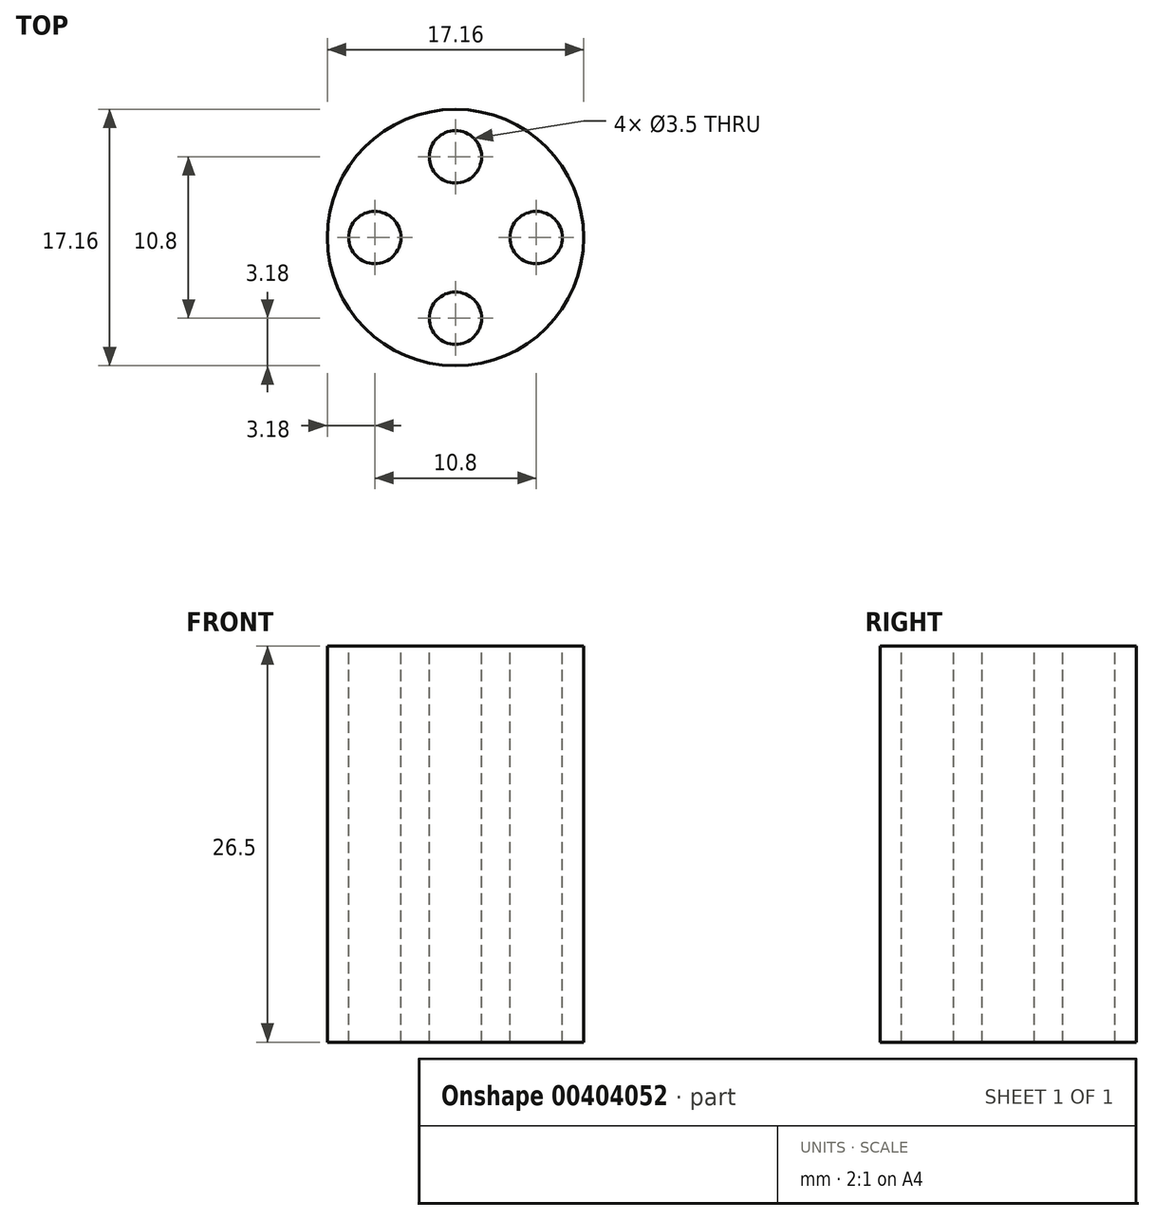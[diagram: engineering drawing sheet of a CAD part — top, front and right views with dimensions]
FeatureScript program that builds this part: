
annotation { "Feature Type Name" : "Feature", "Feature Type Description" : "" }
export const myFeature = defineFeature(function(context is Context, id is Id, definition is map)
    precondition{}
    {
        {
            var Q0;
            Q0=qCreatedBy(makeId("Top.planeOp"),FACE);
            var sketch = newSketch(context, id + "F0", { "sketchPlane" : qUnion([Q0])});
            skCircle(sketch, "E0", {"center": v(0, 0) * mm, "radius": 8.57 * mm});
            skSolve(sketch);
        }
        {
            var Q0;
            Q0 = qSketchRegion(id + "F0", true);
            var Q1;
            Q1=makeQuery(id+"F0.imprint","IMPRINT",FACE,{"disambiguationData":[TD([[makeQuery(id+"F0.imprint","IMPRINT",EDGE,{"derivedFrom":sQuery(id+"F0.wireOp",EDGE,"E0")}),1.0]])]});
            extrude(context, id + "F1", {"entities" : qUnion([Q0, Q1]), "depth" : 26.5 * mm});
        }
        {
            var Q0;
            Q0=makeQuery(id+"F1.opExtrude","CAP_FACE",FACE,{"disambiguationData":[OSD([sQuery(id+"F0.wireOp",EDGE,"E0")])],"isStart":false});
            var sketch = newSketch(context, id + "F2", { "sketchPlane" : qUnion([Q0])});
            skCircle(sketch, "E1", {"center": v(-5.4, 0) * mm, "radius": 0.4 * mm});
            skCircle(sketch, "E2", {"center": v(0, 5.4) * mm, "radius": 0.4 * mm});
            skCircle(sketch, "E3", {"center": v(5.4, 0) * mm, "radius": 0.4 * mm});
            skCircle(sketch, "E4", {"center": v(0, -5.4) * mm, "radius": 0.4 * mm});
            skSolve(sketch);
        }
        {
            var Q0;
            Q0=sQuery(id+"F2.wireOp",VERTEX,"E2.center");
            var Q1;
            Q1=makeQuery(id+"F1.opExtrude","SWEPT_BODY",BODY,{"disambiguationData":[OSD([sQuery(id+"F0.wireOp",EDGE,"E0")])]});
            hole(context, id + "F3", {"style" : HoleStyle.SIMPLE, "endStyle" : HoleEndStyle.THROUGH, "holeDiameter" : 3.5 * mm, "isTappedThrough" : true, "tappedDepth" : 12.7 * mm, "tapClearance" : 3, "locations" : qUnion([Q0]), "scope" : qUnion([Q1])});
        }
        {
            var Q0;
            Q0=sQuery(id+"F2.wireOp",VERTEX,"E3.center");
            var Q1;
            Q1=makeQuery(id+"F1.opExtrude","SWEPT_BODY",BODY,{"disambiguationData":[OSD([sQuery(id+"F0.wireOp",EDGE,"E0")])]});
            hole(context, id + "F4", {"style" : HoleStyle.SIMPLE, "endStyle" : HoleEndStyle.THROUGH, "holeDiameter" : 3.5 * mm, "isTappedThrough" : true, "tappedDepth" : 12.7 * mm, "tapClearance" : 3, "locations" : qUnion([Q0]), "scope" : qUnion([Q1])});
        }
        {
            var Q0;
            Q0=sQuery(id+"F2.wireOp",VERTEX,"E1.center");
            var Q1;
            Q1=sQuery(id+"F2.wireOp",VERTEX,"E4.center");
            var Q2;
            Q2=makeQuery(id+"F1.opExtrude","SWEPT_BODY",BODY,{"disambiguationData":[OSD([sQuery(id+"F0.wireOp",EDGE,"E0")])]});
            hole(context, id + "F5", {"style" : HoleStyle.SIMPLE, "endStyle" : HoleEndStyle.THROUGH, "holeDiameter" : 3.5 * mm, "isTappedThrough" : true, "tappedDepth" : 12.7 * mm, "tapClearance" : 3, "locations" : qUnion([Q0, Q1]), "scope" : qUnion([Q2])});
        }
    });
